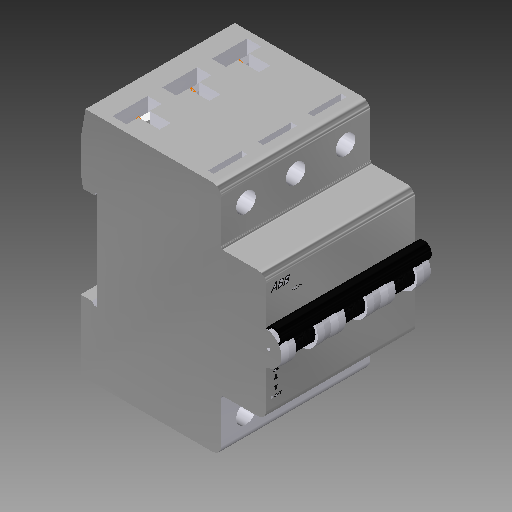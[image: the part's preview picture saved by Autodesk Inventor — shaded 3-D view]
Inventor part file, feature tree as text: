
AUTODESK INVENTOR PART (.ipt)
format: ipt  version: 2017 (Build 210142000, 142)  size: 2,165,248 bytes
history: native  units: mm (DEFAULTED — no unit token found)
features: extrude x18, sketch x14, mirror x13, other x11, chamfer x4, fillet x3, hole x2, shell x1
ambient origin geometry x8: Origin, YZ Plane, XZ Plane, XY Plane, X Axis, Y Axis, Z Axis, Center Point
bodies: Solid1 (feature_tree)
feature tree (66):
  extrude  "Vysunutí1"  Depth=1.0mm
  mirror  "Zrcadlit1"
  chamfer  "Zkosení1"  Distance=60.0mm
  chamfer  "Zkosení2"  Distance=41.5mm
  fillet  "Zaoblení1"  Radius=17.5mm
  extrude  "Vysunutí2"  Depth=22.5mm
  extrude  "Vysunutí3"  Depth=44.0mm
  mirror  "Zrcadlit2"
  hole  "Díra1"  [1 undecoded]
  extrude  "Vysunutí4"  Depth=6.0mm
  mirror  "Zrcadlit3"
  extrude  "Vysunutí5"  Depth=50.0mm
  extrude  "Vysunutí6"  Depth=17.7mm TaperAngle=0.0deg
  extrude  "Vysunutí7"  Depth=10.0mm
  mirror  "Zrcadlit4"
  fillet  "Zaoblení2"  Radius=5.0mm
  fillet  "Zaoblení3"  Radius=3.0mm
  hole  "Díra2"  [1 undecoded]
  mirror  "Zrcadlit5"
  extrude  "Vysunutí8"  Depth=0.5mm
  extrude  "Vysunutí10"  Depth=2.5mm
  mirror  "Zrcadlit8"
  extrude  "Vysunutí11"  Depth=2.5mm TaperAngle=0.0deg
  extrude  "Vysunutí12"  Depth=2.5mm TaperAngle=0.0deg
  mirror  "Zrcadlit9"
  extrude  "Vysunutí13"  Depth=17.5mm TaperAngle=0.0deg
  mirror  "Zrcadlit10"
  extrude  "Vysunutí14"  Depth=17.5mm TaperAngle=0.0deg
  chamfer  "Zkosení3"  Distance=1.5mm
  other  "Závit1"
  chamfer  "Zkosení4"  Distance=1.5mm
  mirror  "Zrcadlit11"
  mirror  "Zrcadlit12"
  extrude  "Vysunutí15"  Depth=6.0mm TaperAngle=0.0deg
  mirror  "Zrcadlit13"
  shell  "Skořepina1"  Thickness=1.0mm
  other  "Reliéf1"
  other  "Reliéf2"
  other  "Reliéf3"
  other  "Reliéf4"
  mirror  "Zrcadlit14"
  extrude  "Vysunutí16"  Depth=3.0mm
  other  "Pracovní rovina5"
  extrude  "Vysunutí19"  Depth=6.0mm
  mirror  "Zrcadlit15"
  extrude  "Vysunutí20"  Depth=8.85mm
  extrude  "Vysunutí21"  Depth=12.0mm
  other  "breaker1"
  other  "breaker2"
  other  "breaker3"
  sketch  "Náčrt5"
  sketch  "Náčrt6"
  sketch  "Náčrt8"
  sketch  "Náčrt9"
  other  "Pracovní rovina1"
  sketch  "Náčrt13"
  sketch  "Náčrt16"
  other  "Pracovní rovina4"
  sketch  "Náčrt18"
  sketch  "Náčrt19"
  sketch  "Náčrt20"
  sketch  "Náčrt21"
  sketch  "Náčrt22"
  sketch  "Náčrt23"
  sketch  "Náčrt26"
  sketch  "Náčrt28"
note: 2 required parameter values undecoded (feature->parameter linkage not recoverable at this tier; creation-order binding heuristic only, values carry confidence <= 0.55)
